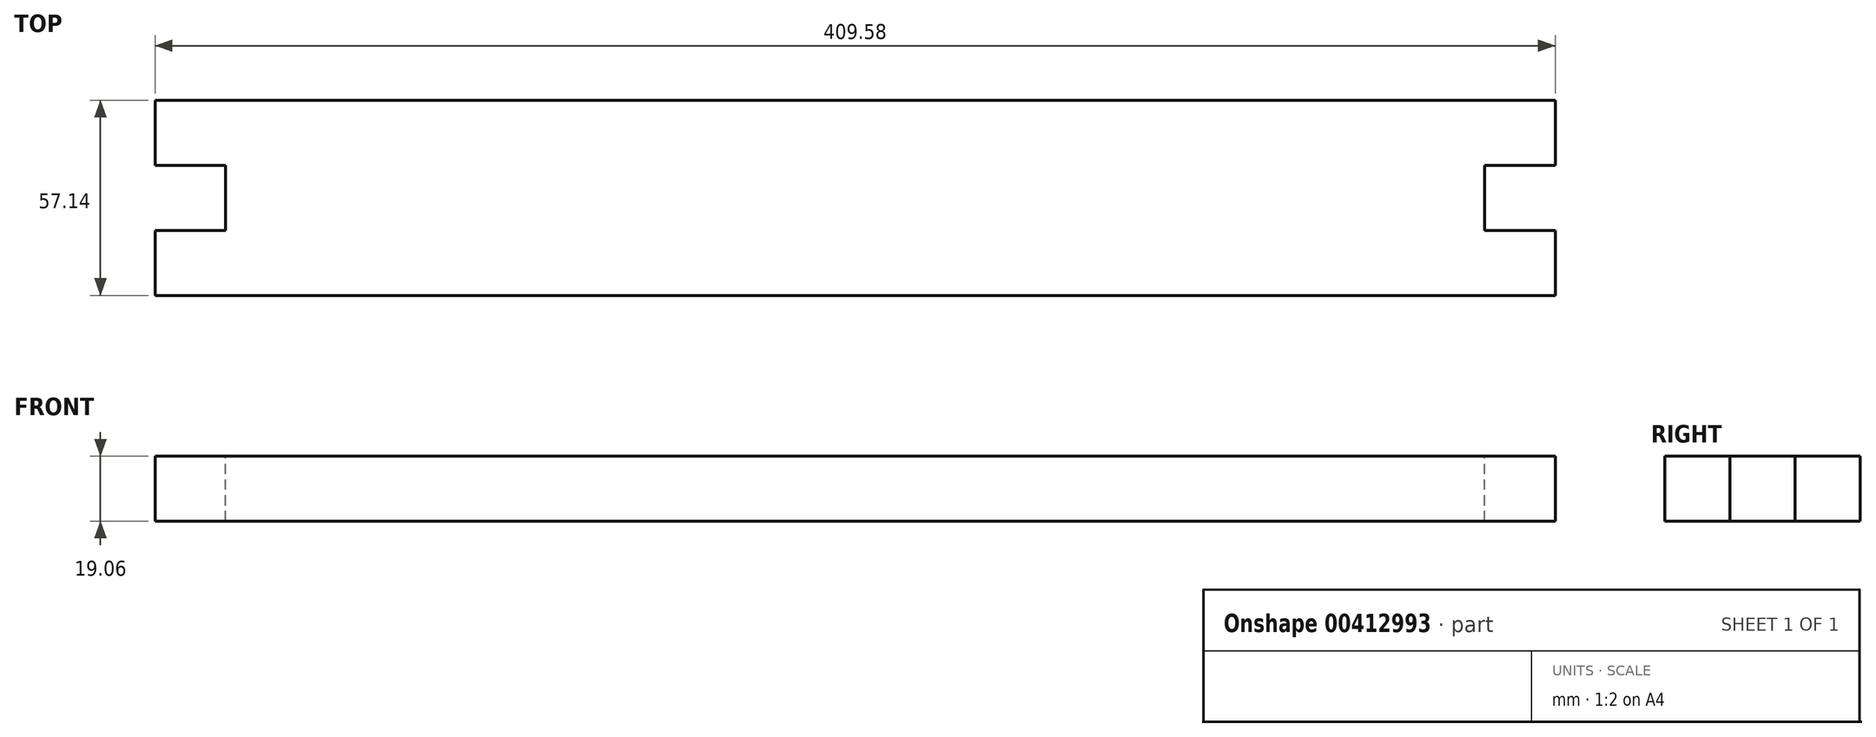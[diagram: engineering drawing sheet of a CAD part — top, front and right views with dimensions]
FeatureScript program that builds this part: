
annotation { "Feature Type Name" : "Feature", "Feature Type Description" : "" }
export const myFeature = defineFeature(function(context is Context, id is Id, definition is map)
    precondition{}
    {
        {
            var Q0;
            Q0=qCreatedBy(makeId("Top.planeOp"),FACE);
            var sketch = newSketch(context, id + "F0", { "sketchPlane" : qUnion([Q0])});
            skLineSegment(sketch, "E0.bottom", {"start": v(-204.79, 28.57) * mm, "end": v(204.79, 28.57) * mm});
            skLineSegment(sketch, "E0.top", {"start": v(-204.79, -28.58) * mm, "end": v(204.79, -28.58) * mm});
            skLineSegment(sketch, "E0.left", {"start": v(-204.79, 28.58) * mm, "end": v(-204.79, -28.58) * mm});
            skLineSegment(sketch, "E0.right", {"start": v(204.79, 28.58) * mm, "end": v(204.79, -28.58) * mm});
            skSolve(sketch);
        }
        {
            var Q0;
            Q0 = qSketchRegion(id + "F0", true);
            extrude(context, id + "F1", {"entities" : qUnion([Q0]), "endBound" : BoundingType.SYMMETRIC, "depth" : 19.05 * mm});
        }
        {
            var Q0;
            Q0=makeQuery(id+"F1.opExtrude","CAP_FACE",FACE,{"disambiguationData":[OSD([sQuery(id+"F0.wireOp",EDGE,"E0.bottom"),sQuery(id+"F0.wireOp",EDGE,"E0.top"),sQuery(id+"F0.wireOp",EDGE,"E0.left"),sQuery(id+"F0.wireOp",EDGE,"E0.right")])],"isStart":false});
            var sketch = newSketch(context, id + "F2", { "sketchPlane" : qUnion([Q0])});
            skLineSegment(sketch, "E1.bottom", {"start": v(-204.79, 9.53) * mm, "end": v(-184.15, 9.52) * mm});
            skLineSegment(sketch, "E1.top", {"start": v(-204.79, -9.52) * mm, "end": v(-184.15, -9.53) * mm});
            skLineSegment(sketch, "E1.left", {"start": v(-204.79, 9.52) * mm, "end": v(-204.79, -9.52) * mm});
            skLineSegment(sketch, "E1.right", {"start": v(-184.15, 9.52) * mm, "end": v(-184.15, -9.52) * mm});
            skLineSegment(sketch, "E2.MirrorCS", {"start": v(204.79, 9.52) * mm, "end": v(204.79, -9.52) * mm});
            skLineSegment(sketch, "E3.MirrorCS", {"start": v(204.79, 9.53) * mm, "end": v(184.15, 9.52) * mm});
            skLineSegment(sketch, "E4.MirrorCS", {"start": v(184.15, 9.52) * mm, "end": v(184.15, -9.52) * mm});
            skLineSegment(sketch, "E5.MirrorCS", {"start": v(204.79, -9.52) * mm, "end": v(184.15, -9.53) * mm});
            skSolve(sketch);
        }
        {
            var Q0;
            Q0 = qSketchRegion(id + "F2", true);
            extrude(context, id + "F3", {"entities" : qUnion([Q0]), "operationType" : NewBodyOperationType.REMOVE, "endBound" : BoundingType.THROUGH_ALL, "oppositeDirection" : true, "depth" : 25.4 * mm});
        }
    });
